# Revit family: FOR UPDATE_71577CHN_NEW
name_source: partatom
category: Plumbing Fixtures
revit_build: Autodesk Revit 2018 (Build: 20170223_1515(x64)
units: mm (PartAtom-declared; Revit-internal decimal feet)

## family parameters
Always vertical = No
Cut with Voids When Loaded = No
OmniClass Number = 23.27.31.29.11
OmniClass Title = Manual Mixing Valves
Part Type = Normal
Room Calculation Point = No
Round Connector Dimension = Use Diameter
Shared = No
Work Plane-Based = Yes

## types (1)
- 71577CHN hansgrohe Basic set for single lever basin mixer for concealed installation wall-mounted
    Always visible = Yes
    BIMobject category = Installation Systems
    Cold Water Inlet = 13 mm
    Cold Water Inlet Description = Cold Water Inlet 12.7mm
    Default Elevation = 1219.2 mm  [stored 4 ft]
    Description = hansgrohe Basic set for single lever basin mixer for concealed installation wall-mounted
    Design country = Germany
    EAN code = 4059625293478
    Edition number = 1
    GTIN code = https://4059625293478
    Hot Water Inlet = 13 mm
    Hot Water Inlet Description = Hot Water Inlet 12.7mm
    IFC Classification = Sanitary Terminal
    Manufacturer = Hansgrohe
    Manufacturer country = Germany
    Manufacturer name = hansgrohe
    Material 1 = Hansgrohe - Plastic - Light khaki
    Material 2 = Hansgrohe - Metal - Brass
    Model = 71577CHN
    OmniClass Code = 23-27 31 29 11
    OmniClass Description = Manual Mixing Valves
    Product Guid = 2c13e508-d3cd-4080-be52-c8b9cf2658ed
    Product SKU = 71577CHN
    Product data url = https://bimobject.com
    Product group = Concealed Basic set washbasin mixer
    Product name = 71577CHN hansgrohe Basic set for single lever basin mixer for concealed installation wall-mounted
    QR code = https://bimobject.com
    URL = https://www.hansgrohe.com
    Weight Net (Kg) = 0.6

note: [stored X ft] marks values corroborated as IEEE doubles in the binary element streams (Revit-internal decimal feet)

## geometry (parser evidence)
native form markers: Sweep x2
no freeform markers — native parametric forms only
